# Revit family: Temp Sensor
name_source: partatom
category: Generic Models
revit_build: Autodesk Revit 2018 (Build: 20190510_1515(x64)
units: mm (PartAtom-declared; Revit-internal decimal feet)

## family parameters
Always vertical = No
Can host rebar = No
Cut with Voids When Loaded = No
OmniClass Number = 23.40.00.00
OmniClass Title = Equipment and Furnishings
Part Type = Normal
Room Calculation Point = No
Round Connector Dimension = Use Diameter
Shared = No
Work Plane-Based = Yes

## types (1)
- Sensors
    BIMObject Category_2 = Sensors
    BIMobject category = Thermostat
    Colour = White RAL 9003
    Connection cable = 2 core cable
    Cost = 34 $
    Current consumption = 10 A
    Default Elevation = 1219 mm
    Depth = 35 mm  [stored 0.114829 ft]
    Design country = UK
    Edition number = 1
    Height = 95 mm
    IFC Classification = Thermostat
    Manufacturer = Easivent
    Manufacturer URL = http://easivent.co.uk
    Manufacturer country = Germany
    Manufacturer name = Siemens
    Material Main = ABS Plastic White
    Model = EV-ITH
    Name of the object = Tamper Proof Thermostat
    Nominal height = 95
    Nominal width = 95
    Notes = Please note this product may be amended without prior notification
    Product SKU = EV-ITH
    Product data URL = http://easivent.co.uk
    Product family = Thermostat
    Product group = Sensors
    SerialNumber = 0
    Size = 95x35x95mm (W x D x H)
    TagNumber = 0
    Technical description = The tamper proof thermostat will be set to the desired corridor temperature, contacts in the thermostat will operate the daily ventilation panel which in turn will instruct the extract fans to run and the relevant AOV to open.

The KSEC 504 is designed for one-person calibration with a unique external 3.5mm jack socket to facilitate direct measurement of the detector output (0-2.5Vdc) using an electrical test meter.
    UNSPSC Code = 41112209
    UNSPSC name = Temperature Sensor
    Uniclass 2.0 Code = PR_30_59_58_88
    Uniclass 2.0 Description = Temperature Sensor
    Voltage = 24V DC
    WarrantyDuration = 12
    WarrantyStartDate = From items dispatch
    Weight Net (Kg) = 0.2
    Width = 95
    switch-on-duration = When temperature exceeds set point

note: [stored X ft] marks values corroborated as IEEE doubles in the binary element streams (Revit-internal decimal feet)

## geometry (parser evidence)
native form markers: Sweep x5
no freeform markers — native parametric forms only
